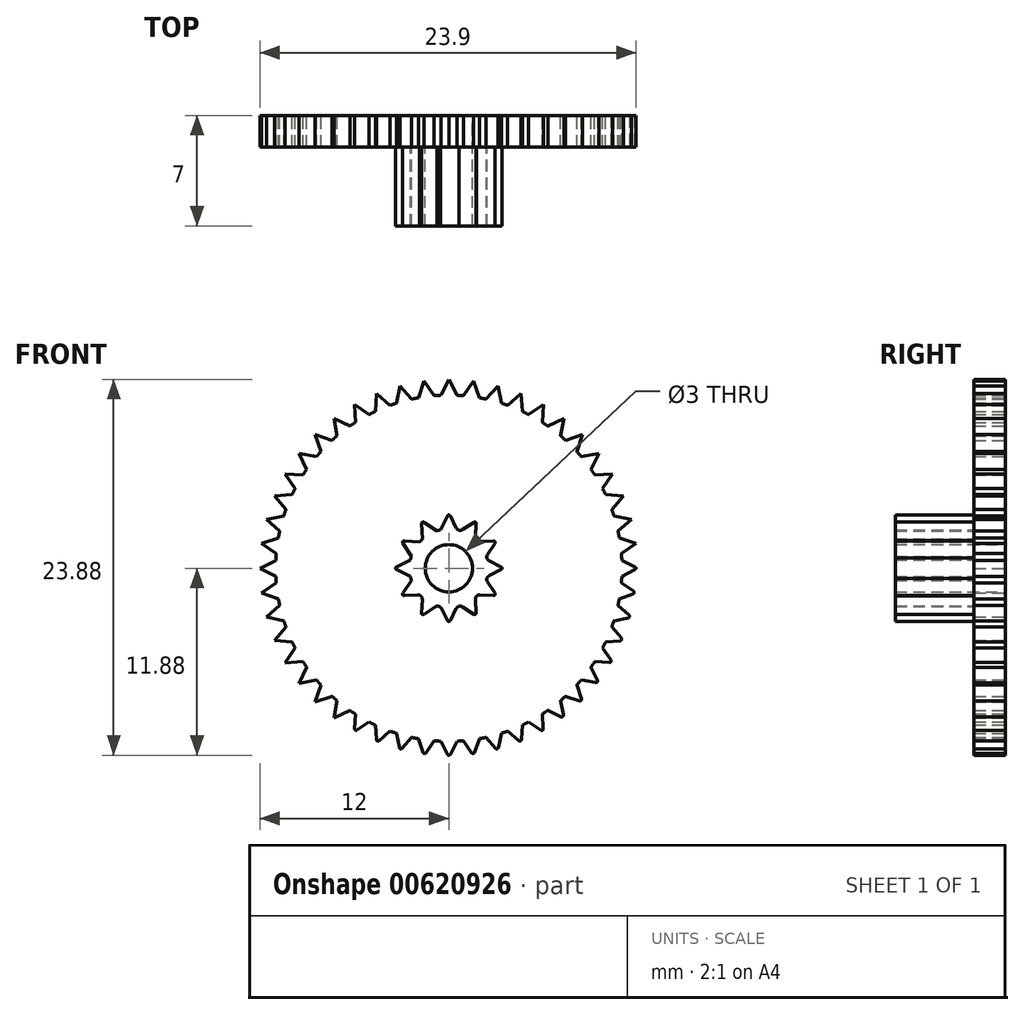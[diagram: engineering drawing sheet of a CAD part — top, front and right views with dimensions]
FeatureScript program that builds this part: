
annotation { "Feature Type Name" : "Feature", "Feature Type Description" : "" }
export const myFeature = defineFeature(function(context is Context, id is Id, definition is map)
    precondition{}
    {
        {
            var Q0;
            Q0=qCreatedBy(makeId("Front.planeOp"),FACE);
            var sketch = newSketch(context, id + "F0", { "sketchPlane" : qUnion([Q0])});
            skCircle(sketch, "E0", {"center": v(0, 0) * mm, "radius": 11 * mm});
            skCircle(sketch, "E1", {"center": v(0, 0) * mm, "radius": 2.5 * mm});
            skCircle(sketch, "E2", {"center": v(0, 0) * mm, "radius": 1.5 * mm});
            skLineSegment(sketch, "E3", {"start": v(0, 11) * mm, "end": v(0, 12) * mm});
            skLineSegment(sketch, "E4", {"start": v(0, 12) * mm, "end": v(-0.51, 10.98) * mm});
            skPoint(sketch, "E5", {"position": v(-0.51, 10.98) * mm});
            skLineSegment(sketch, "E6.MirrorCS", {"start": v(0, 12) * mm, "end": v(0.51, 10.98) * mm});
            skLineSegment(sketch, "E7", {"start": v(0, 12) * mm, "end": v(-0.63, 10.74) * mm});
            skLineSegment(sketch, "E8", {"start": v(0, 12) * mm, "end": v(0.61, 10.78) * mm});
            skLineSegment(sketch, "E9.1.0", {"start": v(-1.57, 11.9) * mm, "end": v(-2.03, 10.57) * mm});
            skLineSegment(sketch, "E9.1.1", {"start": v(-1.57, 11.9) * mm, "end": v(-0.8, 10.77) * mm});
            skLineSegment(sketch, "E9.2.0", {"start": v(-3.1, 11.6) * mm, "end": v(-3.39, 10.21) * mm});
            skLineSegment(sketch, "E9.2.1", {"start": v(-3.1, 11.6) * mm, "end": v(-2.2, 10.57) * mm});
            skLineSegment(sketch, "E9.3.0", {"start": v(-4.6, 11.09) * mm, "end": v(-4.7, 9.68) * mm});
            skLineSegment(sketch, "E9.3.1", {"start": v(-4.6, 11.09) * mm, "end": v(-3.56, 10.2) * mm});
            skLineSegment(sketch, "E9.4.0", {"start": v(-6, 10.4) * mm, "end": v(-5.92, 8.99) * mm});
            skLineSegment(sketch, "E9.4.1", {"start": v(-6, 10.4) * mm, "end": v(-4.86, 9.64) * mm});
            skLineSegment(sketch, "E9.5.0", {"start": v(-7.3, 9.52) * mm, "end": v(-7.04, 8.14) * mm});
            skLineSegment(sketch, "E9.5.1", {"start": v(-7.3, 9.52) * mm, "end": v(-6.08, 8.92) * mm});
            skLineSegment(sketch, "E9.6.0", {"start": v(-8.49, 8.49) * mm, "end": v(-8.04, 7.15) * mm});
            skLineSegment(sketch, "E9.6.1", {"start": v(-8.49, 8.49) * mm, "end": v(-7.2, 8.05) * mm});
            skLineSegment(sketch, "E9.7.0", {"start": v(-9.52, 7.3) * mm, "end": v(-8.9, 6.04) * mm});
            skLineSegment(sketch, "E9.7.1", {"start": v(-9.52, 7.3) * mm, "end": v(-8.18, 7.05) * mm});
            skLineSegment(sketch, "E9.8.0", {"start": v(-10.4, 6) * mm, "end": v(-9.62, 4.83) * mm});
            skLineSegment(sketch, "E9.8.1", {"start": v(-10.4, 6) * mm, "end": v(-9.03, 5.92) * mm});
            skLineSegment(sketch, "E9.9.0", {"start": v(-11.09, 4.6) * mm, "end": v(-10.16, 3.53) * mm});
            skLineSegment(sketch, "E9.9.1", {"start": v(-11.09, 4.6) * mm, "end": v(-9.72, 4.69) * mm});
            skLineSegment(sketch, "E9.10.0", {"start": v(-11.6, 3.1) * mm, "end": v(-10.54, 2.17) * mm});
            skLineSegment(sketch, "E9.10.1", {"start": v(-11.6, 3.1) * mm, "end": v(-10.25, 3.38) * mm});
            skLineSegment(sketch, "E9.11.0", {"start": v(-11.9, 1.57) * mm, "end": v(-10.73, 0.78) * mm});
            skLineSegment(sketch, "E9.11.1", {"start": v(-11.9, 1.57) * mm, "end": v(-10.6, 2.01) * mm});
            skLineSegment(sketch, "E9.12.0", {"start": v(-12, 0) * mm, "end": v(-10.74, -0.63) * mm});
            skLineSegment(sketch, "E9.12.1", {"start": v(-12, 0) * mm, "end": v(-10.78, 0.61) * mm});
            skLineSegment(sketch, "E9.13.0", {"start": v(-11.9, -1.57) * mm, "end": v(-10.57, -2.03) * mm});
            skLineSegment(sketch, "E9.13.1", {"start": v(-11.9, -1.57) * mm, "end": v(-10.77, -0.8) * mm});
            skLineSegment(sketch, "E9.14.0", {"start": v(-11.6, -3.1) * mm, "end": v(-10.21, -3.39) * mm});
            skLineSegment(sketch, "E9.14.1", {"start": v(-11.6, -3.1) * mm, "end": v(-10.57, -2.2) * mm});
            skLineSegment(sketch, "E9.15.0", {"start": v(-11.09, -4.6) * mm, "end": v(-9.68, -4.7) * mm});
            skLineSegment(sketch, "E9.15.1", {"start": v(-11.09, -4.6) * mm, "end": v(-10.2, -3.56) * mm});
            skLineSegment(sketch, "E9.16.0", {"start": v(-10.4, -6) * mm, "end": v(-8.99, -5.92) * mm});
            skLineSegment(sketch, "E9.16.1", {"start": v(-10.4, -6) * mm, "end": v(-9.64, -4.86) * mm});
            skLineSegment(sketch, "E9.17.0", {"start": v(-9.52, -7.3) * mm, "end": v(-8.14, -7.04) * mm});
            skLineSegment(sketch, "E9.17.1", {"start": v(-9.52, -7.3) * mm, "end": v(-8.92, -6.08) * mm});
            skLineSegment(sketch, "E9.18.0", {"start": v(-8.49, -8.49) * mm, "end": v(-7.15, -8.04) * mm});
            skLineSegment(sketch, "E9.18.1", {"start": v(-8.49, -8.49) * mm, "end": v(-8.05, -7.2) * mm});
            skLineSegment(sketch, "E9.19.0", {"start": v(-7.3, -9.52) * mm, "end": v(-6.04, -8.9) * mm});
            skLineSegment(sketch, "E9.19.1", {"start": v(-7.3, -9.52) * mm, "end": v(-7.05, -8.18) * mm});
            skLineSegment(sketch, "E9.20.0", {"start": v(-6, -10.4) * mm, "end": v(-4.83, -9.62) * mm});
            skLineSegment(sketch, "E9.20.1", {"start": v(-6, -10.4) * mm, "end": v(-5.92, -9.03) * mm});
            skLineSegment(sketch, "E9.21.0", {"start": v(-4.6, -11.09) * mm, "end": v(-3.53, -10.16) * mm});
            skLineSegment(sketch, "E9.21.1", {"start": v(-4.6, -11.09) * mm, "end": v(-4.69, -9.72) * mm});
            skLineSegment(sketch, "E9.22.0", {"start": v(-3.1, -11.6) * mm, "end": v(-2.17, -10.54) * mm});
            skLineSegment(sketch, "E9.22.1", {"start": v(-3.1, -11.6) * mm, "end": v(-3.38, -10.25) * mm});
            skLineSegment(sketch, "E9.23.0", {"start": v(-1.57, -11.9) * mm, "end": v(-0.78, -10.73) * mm});
            skLineSegment(sketch, "E9.23.1", {"start": v(-1.57, -11.9) * mm, "end": v(-2.01, -10.6) * mm});
            skLineSegment(sketch, "E9.24.0", {"start": v(0, -12) * mm, "end": v(0.63, -10.74) * mm});
            skLineSegment(sketch, "E9.24.1", {"start": v(0, -12) * mm, "end": v(-0.61, -10.78) * mm});
            skLineSegment(sketch, "E9.25.0", {"start": v(1.57, -11.9) * mm, "end": v(2.03, -10.57) * mm});
            skLineSegment(sketch, "E9.25.1", {"start": v(1.57, -11.9) * mm, "end": v(0.8, -10.77) * mm});
            skLineSegment(sketch, "E9.26.0", {"start": v(3.1, -11.6) * mm, "end": v(3.39, -10.21) * mm});
            skLineSegment(sketch, "E9.26.1", {"start": v(3.1, -11.6) * mm, "end": v(2.2, -10.57) * mm});
            skLineSegment(sketch, "E9.27.0", {"start": v(4.6, -11.09) * mm, "end": v(4.7, -9.68) * mm});
            skLineSegment(sketch, "E9.27.1", {"start": v(4.6, -11.09) * mm, "end": v(3.56, -10.2) * mm});
            skLineSegment(sketch, "E9.28.0", {"start": v(6, -10.4) * mm, "end": v(5.92, -8.99) * mm});
            skLineSegment(sketch, "E9.28.1", {"start": v(6, -10.4) * mm, "end": v(4.86, -9.64) * mm});
            skLineSegment(sketch, "E9.29.0", {"start": v(7.3, -9.52) * mm, "end": v(7.04, -8.14) * mm});
            skLineSegment(sketch, "E9.29.1", {"start": v(7.3, -9.52) * mm, "end": v(6.08, -8.92) * mm});
            skLineSegment(sketch, "E9.30.0", {"start": v(8.49, -8.49) * mm, "end": v(8.04, -7.15) * mm});
            skLineSegment(sketch, "E9.30.1", {"start": v(8.49, -8.49) * mm, "end": v(7.2, -8.05) * mm});
            skLineSegment(sketch, "E9.31.0", {"start": v(9.52, -7.3) * mm, "end": v(8.9, -6.04) * mm});
            skLineSegment(sketch, "E9.31.1", {"start": v(9.52, -7.3) * mm, "end": v(8.18, -7.05) * mm});
            skLineSegment(sketch, "E9.32.0", {"start": v(10.4, -6) * mm, "end": v(9.62, -4.83) * mm});
            skLineSegment(sketch, "E9.32.1", {"start": v(10.4, -6) * mm, "end": v(9.03, -5.92) * mm});
            skLineSegment(sketch, "E9.33.0", {"start": v(11.09, -4.6) * mm, "end": v(10.16, -3.53) * mm});
            skLineSegment(sketch, "E9.33.1", {"start": v(11.09, -4.6) * mm, "end": v(9.72, -4.69) * mm});
            skLineSegment(sketch, "E9.34.0", {"start": v(11.6, -3.1) * mm, "end": v(10.54, -2.17) * mm});
            skLineSegment(sketch, "E9.34.1", {"start": v(11.6, -3.1) * mm, "end": v(10.25, -3.38) * mm});
            skLineSegment(sketch, "E9.35.0", {"start": v(11.9, -1.57) * mm, "end": v(10.73, -0.78) * mm});
            skLineSegment(sketch, "E9.35.1", {"start": v(11.9, -1.57) * mm, "end": v(10.6, -2.01) * mm});
            skLineSegment(sketch, "E9.36.0", {"start": v(12, 0) * mm, "end": v(10.74, 0.63) * mm});
            skLineSegment(sketch, "E9.36.1", {"start": v(12, 0) * mm, "end": v(10.78, -0.61) * mm});
            skLineSegment(sketch, "E9.37.0", {"start": v(11.9, 1.57) * mm, "end": v(10.57, 2.03) * mm});
            skLineSegment(sketch, "E9.37.1", {"start": v(11.9, 1.57) * mm, "end": v(10.77, 0.8) * mm});
            skLineSegment(sketch, "E9.38.0", {"start": v(11.6, 3.1) * mm, "end": v(10.21, 3.39) * mm});
            skLineSegment(sketch, "E9.38.1", {"start": v(11.6, 3.1) * mm, "end": v(10.57, 2.2) * mm});
            skLineSegment(sketch, "E9.39.0", {"start": v(11.09, 4.6) * mm, "end": v(9.68, 4.7) * mm});
            skLineSegment(sketch, "E9.39.1", {"start": v(11.09, 4.6) * mm, "end": v(10.2, 3.56) * mm});
            skLineSegment(sketch, "E9.40.0", {"start": v(10.4, 6) * mm, "end": v(8.99, 5.92) * mm});
            skLineSegment(sketch, "E9.40.1", {"start": v(10.4, 6) * mm, "end": v(9.64, 4.86) * mm});
            skLineSegment(sketch, "E9.41.0", {"start": v(9.52, 7.3) * mm, "end": v(8.14, 7.04) * mm});
            skLineSegment(sketch, "E9.41.1", {"start": v(9.52, 7.3) * mm, "end": v(8.92, 6.08) * mm});
            skLineSegment(sketch, "E9.42.0", {"start": v(8.49, 8.49) * mm, "end": v(7.15, 8.04) * mm});
            skLineSegment(sketch, "E9.42.1", {"start": v(8.49, 8.49) * mm, "end": v(8.05, 7.2) * mm});
            skLineSegment(sketch, "E9.43.0", {"start": v(7.3, 9.52) * mm, "end": v(6.04, 8.9) * mm});
            skLineSegment(sketch, "E9.43.1", {"start": v(7.3, 9.52) * mm, "end": v(7.05, 8.18) * mm});
            skLineSegment(sketch, "E9.44.0", {"start": v(6, 10.4) * mm, "end": v(4.83, 9.62) * mm});
            skLineSegment(sketch, "E9.44.1", {"start": v(6, 10.4) * mm, "end": v(5.92, 9.03) * mm});
            skLineSegment(sketch, "E9.45.0", {"start": v(4.6, 11.09) * mm, "end": v(3.53, 10.16) * mm});
            skLineSegment(sketch, "E9.45.1", {"start": v(4.6, 11.09) * mm, "end": v(4.69, 9.72) * mm});
            skLineSegment(sketch, "E9.46.0", {"start": v(3.1, 11.6) * mm, "end": v(2.17, 10.54) * mm});
            skLineSegment(sketch, "E9.46.1", {"start": v(3.1, 11.6) * mm, "end": v(3.38, 10.25) * mm});
            skLineSegment(sketch, "E9.47.0", {"start": v(1.57, 11.9) * mm, "end": v(0.78, 10.73) * mm});
            skLineSegment(sketch, "E9.47.1", {"start": v(1.57, 11.9) * mm, "end": v(2.01, 10.6) * mm});
            skSolve(sketch);
        }
        {
            var Q0;
            Q0 = qSketchRegion(id + "F0", true);
            extrude(context, id + "F1", {"entities" : qUnion([Q0]), "depth" : 2 * mm, "offsetDistance" : 25 * mm});
        }
        {
            var Q0;
            Q0=qCreatedBy(makeId("Front.planeOp"),FACE);
            var sketch = newSketch(context, id + "F2", { "sketchPlane" : qUnion([Q0])});
            skCircle(sketch, "E10", {"center": v(0, 0) * mm, "radius": 1.5 * mm});
            skCircle(sketch, "E11", {"center": v(0, 0) * mm, "radius": 2.5 * mm});
            skLineSegment(sketch, "E12", {"start": v(0, 2.5) * mm, "end": v(0, 3.5) * mm});
            skLineSegment(sketch, "E13", {"start": v(0, 2.5) * mm, "end": v(0.5, 2.5) * mm});
            skLineSegment(sketch, "E14", {"start": v(0, 3.5) * mm, "end": v(0.56, 2.39) * mm});
            skLineSegment(sketch, "E15.MirrorCS", {"start": v(0, 3.5) * mm, "end": v(-0.56, 2.39) * mm});
            skLineSegment(sketch, "E16.1.0", {"start": v(-1.75, 3.03) * mm, "end": v(-1.68, 1.79) * mm});
            skLineSegment(sketch, "E16.1.1", {"start": v(-1.75, 3.03) * mm, "end": v(-0.71, 2.34) * mm});
            skLineSegment(sketch, "E16.2.0", {"start": v(-3.03, 1.75) * mm, "end": v(-2.34, 0.71) * mm});
            skLineSegment(sketch, "E16.2.1", {"start": v(-3.03, 1.75) * mm, "end": v(-1.79, 1.68) * mm});
            skLineSegment(sketch, "E16.3.0", {"start": v(-3.5, 0) * mm, "end": v(-2.39, -0.56) * mm});
            skLineSegment(sketch, "E16.3.1", {"start": v(-3.5, 0) * mm, "end": v(-2.39, 0.56) * mm});
            skLineSegment(sketch, "E16.4.0", {"start": v(-3.03, -1.75) * mm, "end": v(-1.79, -1.68) * mm});
            skLineSegment(sketch, "E16.4.1", {"start": v(-3.03, -1.75) * mm, "end": v(-2.34, -0.71) * mm});
            skLineSegment(sketch, "E16.5.0", {"start": v(-1.75, -3.03) * mm, "end": v(-0.71, -2.34) * mm});
            skLineSegment(sketch, "E16.5.1", {"start": v(-1.75, -3.03) * mm, "end": v(-1.68, -1.79) * mm});
            skLineSegment(sketch, "E16.6.0", {"start": v(0, -3.5) * mm, "end": v(0.56, -2.39) * mm});
            skLineSegment(sketch, "E16.6.1", {"start": v(0, -3.5) * mm, "end": v(-0.56, -2.39) * mm});
            skLineSegment(sketch, "E16.7.0", {"start": v(1.75, -3.03) * mm, "end": v(1.68, -1.79) * mm});
            skLineSegment(sketch, "E16.7.1", {"start": v(1.75, -3.03) * mm, "end": v(0.71, -2.34) * mm});
            skLineSegment(sketch, "E16.8.0", {"start": v(3.03, -1.75) * mm, "end": v(2.34, -0.71) * mm});
            skLineSegment(sketch, "E16.8.1", {"start": v(3.03, -1.75) * mm, "end": v(1.79, -1.68) * mm});
            skLineSegment(sketch, "E16.9.0", {"start": v(3.5, 0) * mm, "end": v(2.39, 0.56) * mm});
            skLineSegment(sketch, "E16.9.1", {"start": v(3.5, 0) * mm, "end": v(2.39, -0.56) * mm});
            skLineSegment(sketch, "E16.10.0", {"start": v(3.03, 1.75) * mm, "end": v(1.79, 1.68) * mm});
            skLineSegment(sketch, "E16.10.1", {"start": v(3.03, 1.75) * mm, "end": v(2.34, 0.71) * mm});
            skLineSegment(sketch, "E16.11.0", {"start": v(1.75, 3.03) * mm, "end": v(0.71, 2.34) * mm});
            skLineSegment(sketch, "E16.11.1", {"start": v(1.75, 3.03) * mm, "end": v(1.68, 1.79) * mm});
            skSolve(sketch);
        }
        {
            var Q0;
            Q0 = qSketchRegion(id + "F2", true);
            extrude(context, id + "F3", {"entities" : qUnion([Q0]), "operationType" : NewBodyOperationType.ADD, "depth" : 7 * mm, "offsetDistance" : 25 * mm});
        }
        {
            var Q0;
            Q0=makeQuery(id+"F3.opExtrude","SWEPT_EDGE",EDGE,{"disambiguationData":[OSD([sQuery(id+"F2.wireOp",EDGE,"E16.11.0"),sQuery(id+"F2.wireOp",EDGE,"E16.11.1")])]});
            var Q1;
            Q1=makeQuery(id+"F3.opExtrude","SWEPT_EDGE",EDGE,{"disambiguationData":[OSD([sQuery(id+"F2.wireOp",EDGE,"E16.10.0"),sQuery(id+"F2.wireOp",EDGE,"E16.10.1")])]});
            var Q2;
            Q2=makeQuery(id+"F3.opExtrude","SWEPT_EDGE",EDGE,{"disambiguationData":[OSD([sQuery(id+"F2.wireOp",EDGE,"E16.9.0"),sQuery(id+"F2.wireOp",EDGE,"E16.9.1")])]});
            var Q3;
            Q3=makeQuery(id+"F3.opExtrude","SWEPT_EDGE",EDGE,{"disambiguationData":[OSD([sQuery(id+"F2.wireOp",EDGE,"E16.8.0"),sQuery(id+"F2.wireOp",EDGE,"E16.8.1")])]});
            var Q4;
            Q4=makeQuery(id+"F3.opExtrude","SWEPT_EDGE",EDGE,{"disambiguationData":[OSD([sQuery(id+"F2.wireOp",EDGE,"E16.7.0"),sQuery(id+"F2.wireOp",EDGE,"E16.7.1")])]});
            var Q5;
            Q5=makeQuery(id+"F3.opExtrude","SWEPT_EDGE",EDGE,{"disambiguationData":[OSD([sQuery(id+"F2.wireOp",EDGE,"E16.6.0"),sQuery(id+"F2.wireOp",EDGE,"E16.6.1")])]});
            var Q6;
            Q6=makeQuery(id+"F3.opExtrude","SWEPT_EDGE",EDGE,{"disambiguationData":[OSD([sQuery(id+"F2.wireOp",EDGE,"E16.5.0"),sQuery(id+"F2.wireOp",EDGE,"E16.5.1")])]});
            var Q7;
            Q7=makeQuery(id+"F3.opExtrude","SWEPT_EDGE",EDGE,{"disambiguationData":[OSD([sQuery(id+"F2.wireOp",EDGE,"E16.4.0"),sQuery(id+"F2.wireOp",EDGE,"E16.4.1")])]});
            var Q8;
            Q8=makeQuery(id+"F3.opExtrude","SWEPT_EDGE",EDGE,{"disambiguationData":[OSD([sQuery(id+"F2.wireOp",EDGE,"E16.3.0"),sQuery(id+"F2.wireOp",EDGE,"E16.3.1")])]});
            var Q9;
            Q9=makeQuery(id+"F3.opExtrude","SWEPT_EDGE",EDGE,{"disambiguationData":[OSD([sQuery(id+"F2.wireOp",EDGE,"E16.2.0"),sQuery(id+"F2.wireOp",EDGE,"E16.2.1")])]});
            var Q10;
            Q10=makeQuery(id+"F3.opExtrude","SWEPT_EDGE",EDGE,{"disambiguationData":[OSD([sQuery(id+"F2.wireOp",EDGE,"E16.1.0"),sQuery(id+"F2.wireOp",EDGE,"E16.1.1")])]});
            var Q11;
            Q11=makeQuery(id+"F3.opExtrude","SWEPT_EDGE",EDGE,{"disambiguationData":[OSD([sQuery(id+"F2.wireOp",EDGE,"E12"),sQuery(id+"F2.wireOp",EDGE,"E14"),sQuery(id+"F2.wireOp",EDGE,"E15.MirrorCS")])]});
            var Q12;
            Q12=makeQuery(id+"F1.opExtrude","SWEPT_EDGE",EDGE,{"disambiguationData":[OSD([sQuery(id+"F0.wireOp",EDGE,"E9.20.0"),sQuery(id+"F0.wireOp",EDGE,"E9.20.1")])]});
            var Q13;
            Q13=makeQuery(id+"F1.opExtrude","SWEPT_EDGE",EDGE,{"disambiguationData":[OSD([sQuery(id+"F0.wireOp",EDGE,"E9.21.0"),sQuery(id+"F0.wireOp",EDGE,"E9.21.1")])]});
            var Q14;
            Q14=makeQuery(id+"F1.opExtrude","SWEPT_EDGE",EDGE,{"disambiguationData":[OSD([sQuery(id+"F0.wireOp",EDGE,"E9.22.0"),sQuery(id+"F0.wireOp",EDGE,"E9.22.1")])]});
            var Q15;
            Q15=makeQuery(id+"F1.opExtrude","SWEPT_EDGE",EDGE,{"disambiguationData":[OSD([sQuery(id+"F0.wireOp",EDGE,"E9.23.0"),sQuery(id+"F0.wireOp",EDGE,"E9.23.1")])]});
            var Q16;
            Q16=makeQuery(id+"F1.opExtrude","SWEPT_EDGE",EDGE,{"disambiguationData":[OSD([sQuery(id+"F0.wireOp",EDGE,"E9.24.0"),sQuery(id+"F0.wireOp",EDGE,"E9.24.1")])]});
            var Q17;
            Q17=makeQuery(id+"F1.opExtrude","SWEPT_EDGE",EDGE,{"disambiguationData":[OSD([sQuery(id+"F0.wireOp",EDGE,"E9.25.0"),sQuery(id+"F0.wireOp",EDGE,"E9.25.1")])]});
            var Q18;
            Q18=makeQuery(id+"F1.opExtrude","SWEPT_EDGE",EDGE,{"disambiguationData":[OSD([sQuery(id+"F0.wireOp",EDGE,"E9.26.0"),sQuery(id+"F0.wireOp",EDGE,"E9.26.1")])]});
            var Q19;
            Q19=makeQuery(id+"F1.opExtrude","SWEPT_EDGE",EDGE,{"disambiguationData":[OSD([sQuery(id+"F0.wireOp",EDGE,"E9.27.0"),sQuery(id+"F0.wireOp",EDGE,"E9.27.1")])]});
            var Q20;
            Q20=makeQuery(id+"F1.opExtrude","SWEPT_EDGE",EDGE,{"disambiguationData":[OSD([sQuery(id+"F0.wireOp",EDGE,"E9.28.0"),sQuery(id+"F0.wireOp",EDGE,"E9.28.1")])]});
            var Q21;
            Q21=makeQuery(id+"F1.opExtrude","SWEPT_EDGE",EDGE,{"disambiguationData":[OSD([sQuery(id+"F0.wireOp",EDGE,"E9.29.0"),sQuery(id+"F0.wireOp",EDGE,"E9.29.1")])]});
            var Q22;
            Q22=makeQuery(id+"F1.opExtrude","SWEPT_EDGE",EDGE,{"disambiguationData":[OSD([sQuery(id+"F0.wireOp",EDGE,"E9.30.0"),sQuery(id+"F0.wireOp",EDGE,"E9.30.1")])]});
            var Q23;
            Q23=makeQuery(id+"F1.opExtrude","SWEPT_EDGE",EDGE,{"disambiguationData":[OSD([sQuery(id+"F0.wireOp",EDGE,"E9.31.0"),sQuery(id+"F0.wireOp",EDGE,"E9.31.1")])]});
            var Q24;
            Q24=makeQuery(id+"F1.opExtrude","SWEPT_EDGE",EDGE,{"disambiguationData":[OSD([sQuery(id+"F0.wireOp",EDGE,"E9.32.0"),sQuery(id+"F0.wireOp",EDGE,"E9.32.1")])]});
            var Q25;
            Q25=makeQuery(id+"F1.opExtrude","SWEPT_EDGE",EDGE,{"disambiguationData":[OSD([sQuery(id+"F0.wireOp",EDGE,"E9.33.0"),sQuery(id+"F0.wireOp",EDGE,"E9.33.1")])]});
            var Q26;
            Q26=makeQuery(id+"F1.opExtrude","SWEPT_EDGE",EDGE,{"disambiguationData":[OSD([sQuery(id+"F0.wireOp",EDGE,"E9.34.0"),sQuery(id+"F0.wireOp",EDGE,"E9.34.1")])]});
            var Q27;
            Q27=makeQuery(id+"F1.opExtrude","SWEPT_EDGE",EDGE,{"disambiguationData":[OSD([sQuery(id+"F0.wireOp",EDGE,"E9.35.0"),sQuery(id+"F0.wireOp",EDGE,"E9.35.1")])]});
            var Q28;
            Q28=makeQuery(id+"F1.opExtrude","SWEPT_EDGE",EDGE,{"disambiguationData":[OSD([sQuery(id+"F0.wireOp",EDGE,"E9.36.0"),sQuery(id+"F0.wireOp",EDGE,"E9.36.1")])]});
            fillet(context, id + "F4", {"entities" : qUnion([Q0, Q1, Q2, Q3, Q4, Q5, Q6, Q7, Q8, Q9, Q10, Q11, Q12, Q13, Q14, Q15, Q16, Q17, Q18, Q19, Q20, Q21, Q22, Q23, Q24, Q25, Q26, Q27, Q28]), "radius" : .1 * mm, "tangentPropagation" : true, "allowEdgeOverflow" : false});
        }
        {
            var Q0;
            Q0=makeQuery(id+"F3.opExtrude","SWEPT_EDGE",EDGE,{"disambiguationData":[OSD([sQuery(id+"F2.wireOp",EDGE,"E11"),sQuery(id+"F2.wireOp",EDGE,"E14")])]});
            var Q1;
            Q1=makeQuery(id+"F3.opExtrude","SWEPT_EDGE",EDGE,{"disambiguationData":[OSD([sQuery(id+"F2.wireOp",EDGE,"E11"),sQuery(id+"F2.wireOp",EDGE,"E16.11.0")])]});
            var Q2;
            Q2=makeQuery(id+"F3.opExtrude","SWEPT_EDGE",EDGE,{"disambiguationData":[OSD([sQuery(id+"F2.wireOp",EDGE,"E11"),sQuery(id+"F2.wireOp",EDGE,"E16.11.1")])]});
            var Q3;
            Q3=makeQuery(id+"F3.opExtrude","SWEPT_EDGE",EDGE,{"disambiguationData":[OSD([sQuery(id+"F2.wireOp",EDGE,"E11"),sQuery(id+"F2.wireOp",EDGE,"E16.10.0")])]});
            var Q4;
            Q4=makeQuery(id+"F3.opExtrude","SWEPT_EDGE",EDGE,{"disambiguationData":[OSD([sQuery(id+"F2.wireOp",EDGE,"E11"),sQuery(id+"F2.wireOp",EDGE,"E16.10.1")])]});
            var Q5;
            Q5=makeQuery(id+"F3.opExtrude","SWEPT_EDGE",EDGE,{"disambiguationData":[OSD([sQuery(id+"F2.wireOp",EDGE,"E11"),sQuery(id+"F2.wireOp",EDGE,"E16.9.0")])]});
            var Q6;
            Q6=makeQuery(id+"F3.opExtrude","SWEPT_EDGE",EDGE,{"disambiguationData":[OSD([sQuery(id+"F2.wireOp",EDGE,"E11"),sQuery(id+"F2.wireOp",EDGE,"E16.9.1")])]});
            var Q7;
            Q7=makeQuery(id+"F3.opExtrude","SWEPT_EDGE",EDGE,{"disambiguationData":[OSD([sQuery(id+"F2.wireOp",EDGE,"E11"),sQuery(id+"F2.wireOp",EDGE,"E16.8.0")])]});
            var Q8;
            Q8=makeQuery(id+"F3.opExtrude","SWEPT_EDGE",EDGE,{"disambiguationData":[OSD([sQuery(id+"F2.wireOp",EDGE,"E11"),sQuery(id+"F2.wireOp",EDGE,"E16.8.1")])]});
            var Q9;
            Q9=makeQuery(id+"F3.opExtrude","SWEPT_EDGE",EDGE,{"disambiguationData":[OSD([sQuery(id+"F2.wireOp",EDGE,"E11"),sQuery(id+"F2.wireOp",EDGE,"E16.7.0")])]});
            var Q10;
            Q10=makeQuery(id+"F3.opExtrude","SWEPT_EDGE",EDGE,{"disambiguationData":[OSD([sQuery(id+"F2.wireOp",EDGE,"E11"),sQuery(id+"F2.wireOp",EDGE,"E16.7.1")])]});
            var Q11;
            Q11=makeQuery(id+"F3.opExtrude","SWEPT_EDGE",EDGE,{"disambiguationData":[OSD([sQuery(id+"F2.wireOp",EDGE,"E11"),sQuery(id+"F2.wireOp",EDGE,"E16.6.0")])]});
            var Q12;
            Q12=makeQuery(id+"F3.opExtrude","SWEPT_EDGE",EDGE,{"disambiguationData":[OSD([sQuery(id+"F2.wireOp",EDGE,"E11"),sQuery(id+"F2.wireOp",EDGE,"E16.6.1")])]});
            var Q13;
            Q13=makeQuery(id+"F3.opExtrude","SWEPT_EDGE",EDGE,{"disambiguationData":[OSD([sQuery(id+"F2.wireOp",EDGE,"E11"),sQuery(id+"F2.wireOp",EDGE,"E16.5.0")])]});
            var Q14;
            Q14=makeQuery(id+"F3.opExtrude","SWEPT_EDGE",EDGE,{"disambiguationData":[OSD([sQuery(id+"F2.wireOp",EDGE,"E11"),sQuery(id+"F2.wireOp",EDGE,"E16.5.1")])]});
            var Q15;
            Q15=makeQuery(id+"F3.opExtrude","SWEPT_EDGE",EDGE,{"disambiguationData":[OSD([sQuery(id+"F2.wireOp",EDGE,"E11"),sQuery(id+"F2.wireOp",EDGE,"E16.4.0")])]});
            fillet(context, id + "F5", {"entities" : qUnion([Q0, Q1, Q2, Q3, Q4, Q5, Q6, Q7, Q8, Q9, Q10, Q11, Q12, Q13, Q14, Q15]), "radius" : .3 * mm, "tangentPropagation" : true, "allowEdgeOverflow" : false});
        }
    });
